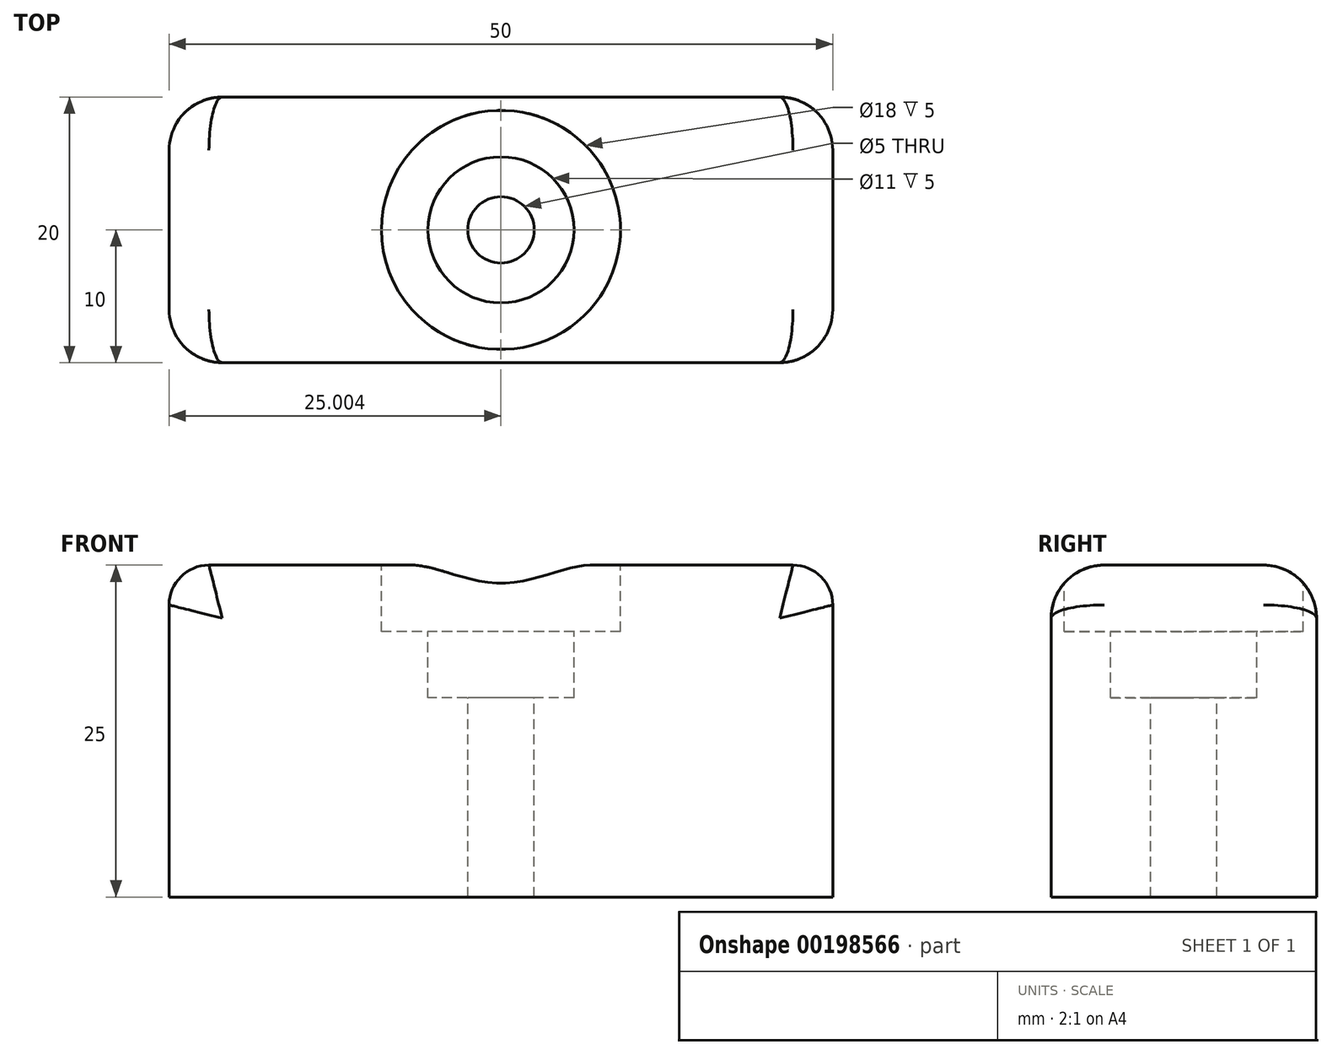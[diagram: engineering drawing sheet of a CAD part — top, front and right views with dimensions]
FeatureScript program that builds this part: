
annotation { "Feature Type Name" : "Feature", "Feature Type Description" : "" }
export const myFeature = defineFeature(function(context is Context, id is Id, definition is map)
    precondition{}
    {
        {
            var Q0;
            Q0=qCreatedBy(makeId("Top.planeOp"),FACE);
            var sketch = newSketch(context, id + "F0", { "sketchPlane" : qUnion([Q0])});
            skLineSegment(sketch, "E0.bottom", {"start": v(18.74, 16.83) * mm, "end": v(-31.26, 16.83) * mm});
            skLineSegment(sketch, "E0.top", {"start": v(18.74, -3.17) * mm, "end": v(-31.26, -3.17) * mm});
            skLineSegment(sketch, "E0.left", {"start": v(18.74, 16.83) * mm, "end": v(18.74, -3.17) * mm});
            skLineSegment(sketch, "E0.right", {"start": v(-31.26, 16.83) * mm, "end": v(-31.26, -3.17) * mm});
            skSolve(sketch);
        }
        {
            var Q0;
            Q0 = qSketchRegion(id + "F0", true);
            extrude(context, id + "F1", {"entities" : qUnion([Q0]), "depth" : 25 * mm});
        }
        {
            var Q0;
            Q0=makeQuery(id+"F1.opExtrude","CAP_FACE",FACE,{"disambiguationData":[OSD([sQuery(id+"F0.wireOp",EDGE,"E0.bottom"),sQuery(id+"F0.wireOp",EDGE,"E0.top"),sQuery(id+"F0.wireOp",EDGE,"E0.left"),sQuery(id+"F0.wireOp",EDGE,"E0.right")])],"isStart":false});
            var sketch = newSketch(context, id + "F2", { "sketchPlane" : qUnion([Q0])});
            skCircle(sketch, "E1", {"center": v(-6.26, 6.83) * mm, "radius": 9 * mm});
            skPoint(sketch, "E1.centerSnap0", {"position": v(-6.26, 16.83) * mm});
            skPoint(sketch, "E1.centerSnap1", {"position": v(-31.26, 6.83) * mm});
            skSolve(sketch);
        }
        {
            var Q0;
            Q0 = qSketchRegion(id + "F2", true);
            extrude(context, id + "F3", {"entities" : qUnion([Q0]), "operationType" : NewBodyOperationType.REMOVE, "oppositeDirection" : true, "depth" : 5 * mm});
        }
        {
            var Q0;
            Q0=makeQuery(id+"F3.boolean.opBoolean","COPY",FACE,{"derivedFrom":makeQuery(id+"F3.opExtrude","CAP_FACE",FACE,{"disambiguationData":[OSD([sQuery(id+"F2.wireOp",EDGE,"E1")])],"isStart":false})});
            var sketch = newSketch(context, id + "F4", { "sketchPlane" : qUnion([Q0])});
            skPoint(sketch, "E2", {"position": v(-6.26, 6.83) * mm});
            skSolve(sketch);
        }
        {
            var Q0;
            Q0=sQuery(id+"F4.wireOp",VERTEX,"E2");
            var Q1;
            Q1=makeQuery(id+"F1.opExtrude","SWEPT_BODY",BODY,{"disambiguationData":[OSD([sQuery(id+"F0.wireOp",EDGE,"E0.bottom"),sQuery(id+"F0.wireOp",EDGE,"E0.top"),sQuery(id+"F0.wireOp",EDGE,"E0.left"),sQuery(id+"F0.wireOp",EDGE,"E0.right")])]});
            hole(context, id + "F5", {"style" : HoleStyle.C_BORE, "endStyle" : HoleEndStyle.THROUGH, "holeDiameter" : 5 * mm, "cBoreDiameter" : 11 * mm, "cBoreDepth" : 5 * mm, "startFromSketch" : true, "locations" : qUnion([Q0]), "scope" : qUnion([Q1]), "isTappedThrough" : true});
        }
        {
            var Q0;
            Q0=makeQuery(id+"F1.opExtrude","SWEPT_EDGE",EDGE,{"disambiguationData":[OSD([sQuery(id+"F0.wireOp",EDGE,"E0.bottom"),sQuery(id+"F0.wireOp",EDGE,"E0.right")])]});
            var Q1;
            Q1=makeQuery(id+"F1.opExtrude","SWEPT_EDGE",EDGE,{"disambiguationData":[OSD([sQuery(id+"F0.wireOp",EDGE,"E0.bottom"),sQuery(id+"F0.wireOp",EDGE,"E0.left")])]});
            var Q2;
            Q2=makeQuery(id+"F1.opExtrude","SWEPT_EDGE",EDGE,{"disambiguationData":[OSD([sQuery(id+"F0.wireOp",EDGE,"E0.top"),sQuery(id+"F0.wireOp",EDGE,"E0.left")])]});
            var Q3;
            Q3=makeQuery(id+"F1.opExtrude","SWEPT_EDGE",EDGE,{"disambiguationData":[OSD([sQuery(id+"F0.wireOp",EDGE,"E0.top"),sQuery(id+"F0.wireOp",EDGE,"E0.right")])]});
            var Q4;
            Q4=makeQuery(id+"F1.opExtrude","CAP_EDGE",EDGE,{"disambiguationData":[OSD([sQuery(id+"F0.wireOp",EDGE,"E0.top")])],"isStart":false});
            var Q5;
            Q5=makeQuery(id+"F1.opExtrude","CAP_EDGE",EDGE,{"disambiguationData":[OSD([sQuery(id+"F0.wireOp",EDGE,"E0.bottom")])],"isStart":false});
            fillet(context, id + "F6", {"entities" : qUnion([Q0, Q1, Q2, Q3, Q4, Q5]), "radius" : 4 * mm, "tangentPropagation" : true, "allowEdgeOverflow" : false});
        }
        {
            var Q0;
            Q0=makeQuery(id+"F1.opExtrude","CAP_EDGE",EDGE,{"disambiguationData":[OSD([sQuery(id+"F0.wireOp",EDGE,"E0.left")])],"isStart":false});
            var Q1;
            Q1=makeQuery(id+"F1.opExtrude","CAP_EDGE",EDGE,{"disambiguationData":[OSD([sQuery(id+"F0.wireOp",EDGE,"E0.right")])],"isStart":false});
            fillet(context, id + "F7", {"entities" : qUnion([Q0, Q1]), "radius" : 3 * mm, "tangentPropagation" : true, "allowEdgeOverflow" : false});
        }
    });
